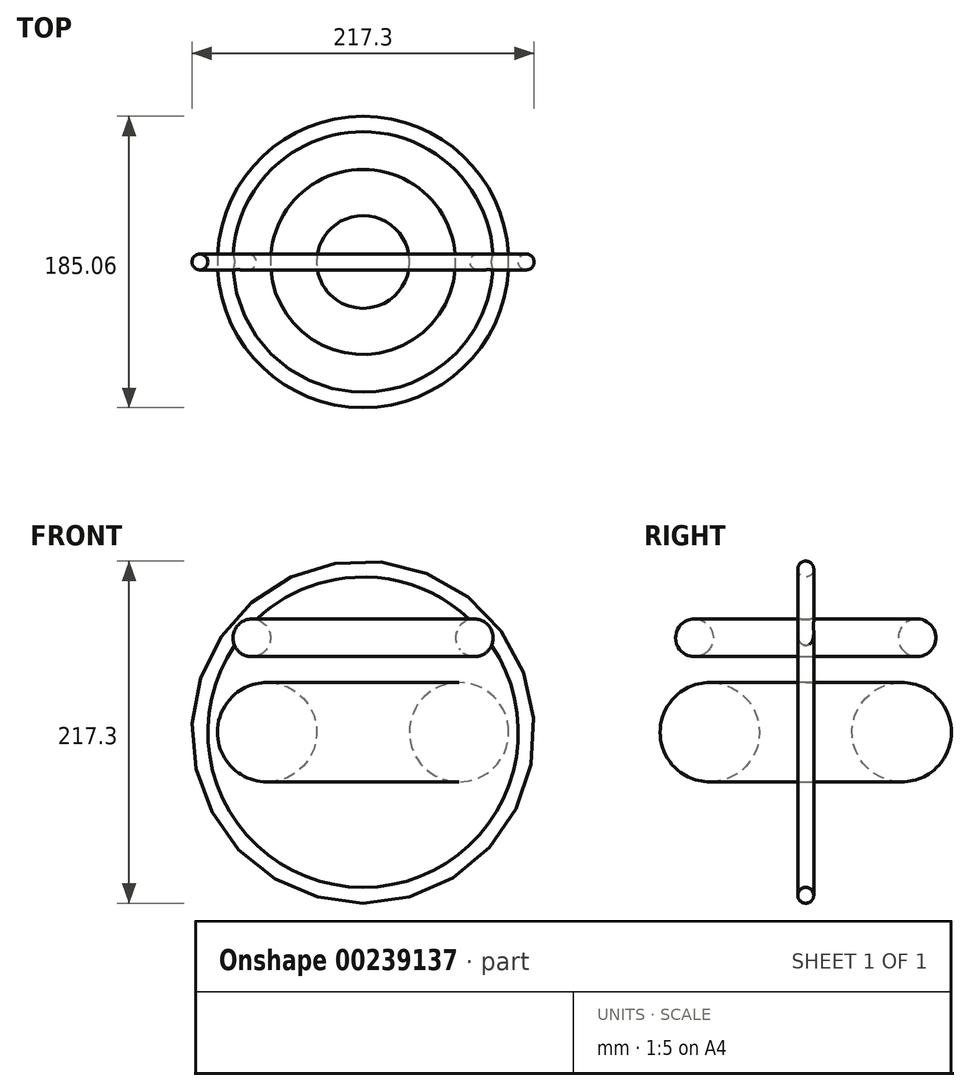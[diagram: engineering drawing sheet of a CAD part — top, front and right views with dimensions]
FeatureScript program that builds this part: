
annotation { "Feature Type Name" : "Feature", "Feature Type Description" : "" }
export const myFeature = defineFeature(function(context is Context, id is Id, definition is map)
    precondition{}
    {
        {
            var Q0;
            Q0=qCreatedBy(makeId("Front.planeOp"),FACE);
            var sketch = newSketch(context, id + "F0", { "sketchPlane" : qUnion([Q0])});
            skCircle(sketch, "E0", {"center": v(60.98, 0) * mm, "radius": 31.55 * mm});
            skLineSegment(sketch, "E1", {"start": v(0, 45.05) * mm, "end": v(0, -45.05) * mm, "construction": true});
            skSolve(sketch);
        }
        {
            var Q0;
            Q0 = qSketchRegion(id + "F0", true);
            var Q1;
            Q1=sQuery(id+"F0.wireOp",EDGE,"E1");
            revolve(context, id + "F1", {"entities" : qUnion([Q0]), "axis" : qUnion([Q1]), "revolveType" : RevolveType.FULL});
        }
        {
            var Q0;
            Q0=qCreatedBy(makeId("Front.planeOp"),FACE);
            var sketch = newSketch(context, id + "F2", { "sketchPlane" : qUnion([Q0])});
            skLineSegment(sketch, "E2", {"start": v(0, 66.91) * mm, "end": v(0, 49.98) * mm, "construction": true});
            skCircle(sketch, "E3", {"center": v(70.73, 59.94) * mm, "radius": 11.96 * mm});
            skSolve(sketch);
        }
        {
            var Q0;
            Q0 = qSketchRegion(id + "F2", true);
            var Q1;
            Q1=sQuery(id+"F2.wireOp",EDGE,"E2");
            revolve(context, id + "F3", {"entities" : qUnion([Q0]), "axis" : qUnion([Q1]), "revolveType" : RevolveType.FULL});
        }
        {
            var Q0;
            Q0=qCreatedBy(makeId("Top.planeOp"),FACE);
            var sketch = newSketch(context, id + "F4", { "sketchPlane" : qUnion([Q0])});
            skLineSegment(sketch, "E4", {"start": v(0, 24.4) * mm, "end": v(0, -21.09) * mm, "construction": true});
            skCircle(sketch, "E5", {"center": v(103.6, 0) * mm, "radius": 5.05 * mm});
            skSolve(sketch);
        }
        {
            var Q0;
            Q0 = qSketchRegion(id + "F4", true);
            var Q1;
            Q1=sQuery(id+"F4.wireOp",EDGE,"E4");
            revolve(context, id + "F5", {"operationType" : NewBodyOperationType.ADD, "entities" : qUnion([Q0]), "axis" : qUnion([Q1]), "revolveType" : RevolveType.FULL});
        }
    });
